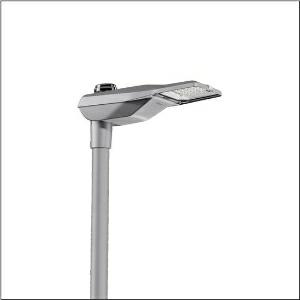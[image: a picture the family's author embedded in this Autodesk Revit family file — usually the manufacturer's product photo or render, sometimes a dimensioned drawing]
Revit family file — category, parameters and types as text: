
# Revit family: streetlight_sl_21_micro___stw1_0a_5xe5e47n08db_5020
name_source: partatom
category: Lighting Fixtures
units: mm (PartAtom-declared; Revit-internal decimal feet)

## family parameters
Cut with Voids When Loaded = No
Host = Face
Light Source = No
Part Type = Normal
Room Calculation Point = No
Round Connector Dimension = Use Diameter
Shared = No

## types (1)
- --- (1 x LED, 5320 lm, 39.1 W, 4000K)
    Apparent Load = 39 VA
    CIE Flux Codes = 38 75 98 100 100
    Color Rendering = 70
    Color Temperature = 4000K
    Default Elevation = 1800 mm
    Description = Streetlight SL 21 micro, mast luminaire, primary light control with lens, of PMMA, primary optical cover: cover, of toughened safety glass, transparent, light distribution: STW1.0a, light emission: direct distribution, primary light characteristic: asymmetric, installation type: post-top, LED, 3G 1.5mm², High Power LED, rated luminous flux: 5.320lm, luminous efficacy: 136lm/W, light colour: 740, colour temperature: 4000K, control gear: NEMA (7pin), control: overheat protection, pre-setting: linear dimming characteristic, constant luminous flux control, time-dependent luminous flux control, flexible luminous flux parameterisation, mains connection: 230..240V, AC, 50/60Hz, connection cable pre-assembled, cable length: 6,5m, wiring characteristics: H07RN-F, start of lifetime: 39W, end of service life: 41W, reduction: 18W, luminaire housing, of diecast aluminium (EN AC-44300), powder-coated, SITECO metallic grey (DB 702S), corrosivity category C5 high according to DIN EN ISO 12944, multi-level sealing system, sealing non-destructively replaceable, inclination adjustable: 0°, 5°, 10°, 15°, length: 528mm, width: 235mm, height: 110mm, spigot size: 76/60mm (post-top), mounting height: 4..8m, protection rating (complete): IP66, insulation class (complete): insulation class I (protective earthing), certification: CE, ENEC, ENEC+, VDE, impact resistance: IK10, permissible operating ambient temperature for outdoor applications: -40..+50°C, standard-compliant lighting for roads and squares, packaging unit: 1 piece

Light Distribution: STW1.0a
    Height = 110 mm
    Lamp = 1 x LED
    Lamp Light Flux = 5320 lm
    Lamp Power = 39.1 W
    Lamp count = 1
    Length = 528 mm
    Luminous efficacy = 136 lm/W
    Manufacturer = Siteco
    ModVariant = No
    Model = 5XE5E47N08DB
    Number of Poles = 1
    OnlyDefault = Yes
    Power Factor = 1
    Product Name = Streetlight SL 21 micro | STW1.0a
    Product group = mast luminaire | pylon top
    ProductGroupID = 6100
    Protection Class = Protection class I
    Protection Degree = IP 66
    RLX_Detail_Level = 1
    RLX_Emergency_Light_Flux = 0 lm
    RLX_Emergency_Type = 0
    RLX_Emergency_Type_DB = No
    RlxData = <blob elided: 98969 chars, md5=ce07b96f>
    Socket = socket
    Standby Power = 0 W
    System Light Flux = 5320 lm
    System Power = 39 W
    Type Comments = factory setting: luminous flux: 100 % | dim-lin: 254 | 765 mA
    Type Image = l_1294375.jpg
    URL = http://relux.com
    VarID = @adj_135249
    Voltage = 0 V
    Weight = 0.00 kg
    Width = 235 mm

## geometry (parser evidence)
native form markers: Blend x4, Sweep x10
no freeform markers — native parametric forms only
